# Revit family: TD92_ALB750_VER020_RVT20_R00
name_source: partatom
category: Mobiliário
units: mm (PartAtom-declared; Revit-internal decimal feet)

## family parameters
Com base no plano de trabalho = Não
Compartilhado = Não
Corte com vazios quando carregada = Não
Número OmniClass = 23.40.20.00
Ponto de cálculo do ambiente = Não
Sempre na vertical = Sim
Título OmniClass = General Furniture and Specialties

## types (1)
- TD92_ALB750_VER020_RVT20_R00
    Descrição = Além de atender às suas necessidade, essa peça é um coringa na decoração. O Cabideiro Tramontina Albero em Polietileno vai trazer muito mais estilo na composição da sua decoração, além de cumprir sua função com muita praticidade e versatilidade.
    Elevação padrão = 0  [stored 0 ft]
    Fabricante = Tramontina Delta S/A
    Modelo = Cabideiro Tramontina Albero em Polietileno Verde
    Nota-chave = 92750020
    URL = https://www.tramontinastore.com

note: [stored X ft] marks values corroborated as IEEE doubles in the binary element streams (Revit-internal decimal feet)
